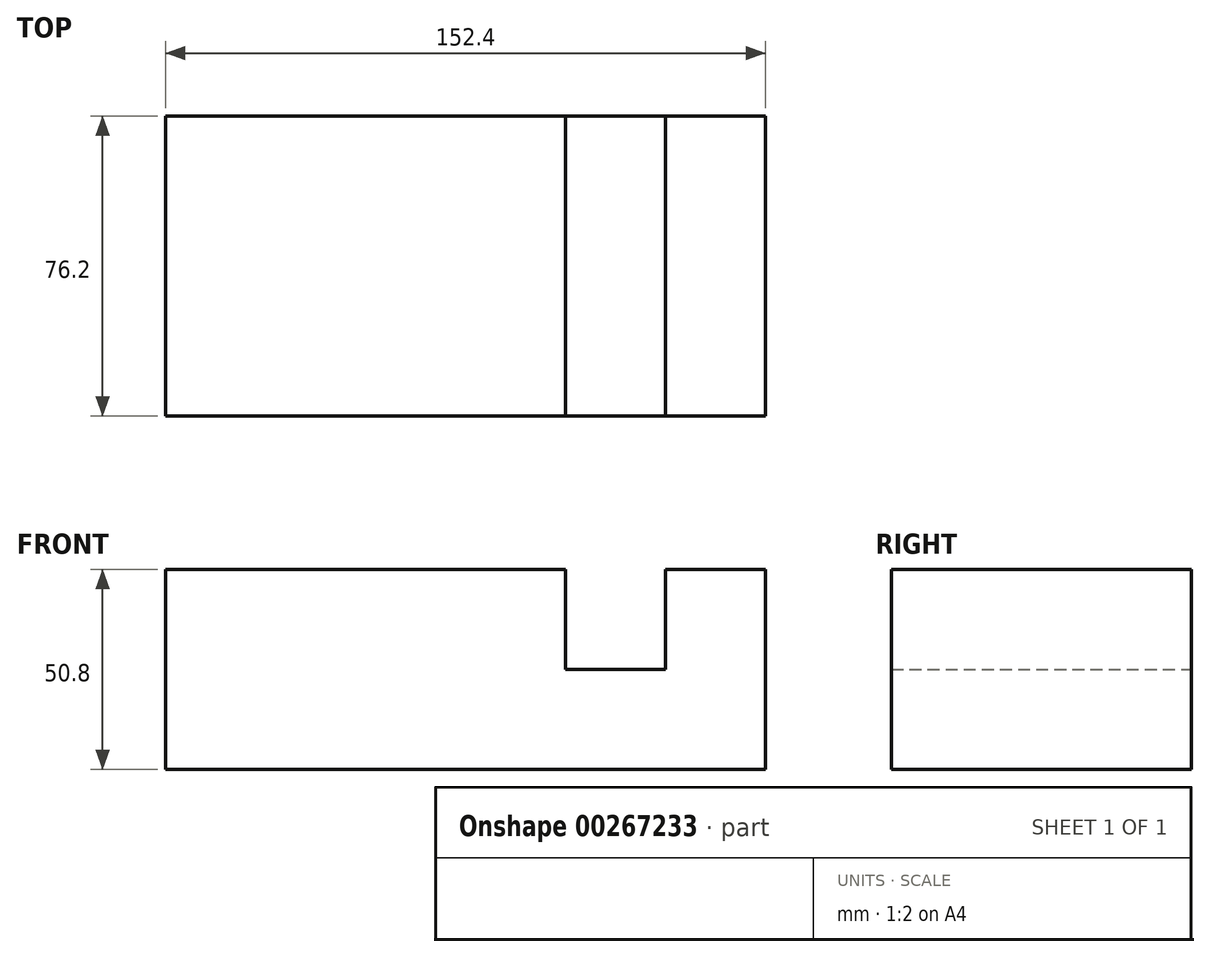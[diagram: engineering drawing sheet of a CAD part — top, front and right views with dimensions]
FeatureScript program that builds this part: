
annotation { "Feature Type Name" : "Feature", "Feature Type Description" : "" }
export const myFeature = defineFeature(function(context is Context, id is Id, definition is map)
    precondition{}
    {
        {
            var Q0;
            Q0=qCreatedBy(makeId("Front.planeOp"),FACE);
            var sketch = newSketch(context, id + "F0", { "sketchPlane" : qUnion([Q0])});
            skLineSegment(sketch, "E0", {"start": v(0, 0) * mm, "end": v(0, -50.8) * mm});
            skLineSegment(sketch, "E1", {"start": v(0, -50.8) * mm, "end": v(152.4, -50.8) * mm});
            skLineSegment(sketch, "E2", {"start": v(152.4, -50.8) * mm, "end": v(152.4, 0) * mm});
            skLineSegment(sketch, "E3", {"start": v(152.4, 0) * mm, "end": v(127, 0) * mm});
            skLineSegment(sketch, "E4", {"start": v(127, 0) * mm, "end": v(127, -25.4) * mm});
            skLineSegment(sketch, "E5", {"start": v(127, -25.4) * mm, "end": v(101.6, -25.4) * mm});
            skLineSegment(sketch, "E6", {"start": v(101.6, -25.4) * mm, "end": v(101.6, 0) * mm});
            skLineSegment(sketch, "E7", {"start": v(101.6, 0) * mm, "end": v(-4.46, 0) * mm});
            skSolve(sketch);
        }
        {
            var Q0;
            {var subQ0=sQuery(id+"F0.wireOp",EDGE,"E0");Q0=makeQuery(id+"F0.imprint","IMPRINT",FACE,{"disambiguationData":[TD([[makeQuery(id+"F0.imprint","IMPRINT",EDGE,{"derivedFrom":subQ0}),1.0]])]});}
            extrude(context, id + "F1", {"entities" : qUnion([Q0]), "depth" : 76.2 * mm});
        }
    });
